# Revit family: 12990_without trims
name_source: partatom
category: Specialty Equipment
units: mm (PartAtom-declared; Revit-internal decimal feet)

## family parameters
Always vertical = Yes
Cut with Voids When Loaded = No
Enable Cutting in Views = Yes
Host = Wall
Maintain Annotation Orientation = No
Part Type = Normal
Room Calculation Point = No
Round Connector Dimension = Use Diameter
Shared = No

## types (2) — shared parameters
Placement from front = 52 mm
Void width = 620 mm  [stored 2.03412 ft]
zero-valued in all types: Default Elevation

## per-type parameters (varying)
- Visio Uniq model: BIMobject category=Gas - Fireplaces; Chimney connection=200 mm. Diameter; Description information=RAIS Visio 70 3S has front glass of 70 cm and glass on three sides. With this gas fireplace you can enjoy the fire from all sides. A discreet frame frames the fire so that the flames are really in focus. The gas fireplace has an incredibly lifelike and authentic flame image, which is controlled by remote control or your phone/tablet.

This model is available with a black or stainless steel frame.

Can be connected to natural gas, city gas, LPG or biogas.; Design and manufacturer country=Denmark; Distance to combustible material (ceiling)=Min. 420 mm.; Distance to combustible material (floor)=Min. 375 mm.; Distance to combustible material from glass=Min. 700 mm.; Edition number=1; IFC classification=Object; Manufacturer=RAIS A/S; Manufacturer name=Visio Uniq model; Materiale frame=Without frame; OmniClass Code=23-19 17 00; OmniClass Description=Fireplaces; Product data url=BIM Link; Product family=Visio Uniq model; Product group=Fireplace; Product name=Rais Visio Uniq model 3S; Product url=https://www.rais.com; QR Code=BIM link; URL=https://www.rais.com; UniClass 1.4 Code=L828; UniClass 1.4 Description=Fireplaces; UniClass 2.0 Code=Pr_70_60_82_30; UniClass 2.0 Description=Fireplaces hearth
- Visio 70-43-39-3S Gas: Distance to combustible material (floor)=Min. 1000 mm.; Distance to combustible material from glass=Min. 150 mm.; Edition number=Denmark; IFC classification=Gas - Fireplaces; Manufacturer name=1; OmniClass Code=Object; OmniClass Description=23-19 17 00; Product SKU=Rais Visio 70 3S; Product family=Visio 3S - Gas; Product group=Visio 3S; Product name=Gas - Fireplace; UniClass 1.4 Code=Fireplaces; UniClass 1.4 Description=Pr_70_60_82_30; UniClass 2.0 Code=Fireplaces hearth; UniClass 2.0 Description=Pr_70_60_82_30

note: [stored X ft] marks values corroborated as IEEE doubles in the binary element streams (Revit-internal decimal feet)

## geometry (parser evidence)
native form markers: Sweep x4
no freeform markers — native parametric forms only
